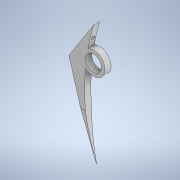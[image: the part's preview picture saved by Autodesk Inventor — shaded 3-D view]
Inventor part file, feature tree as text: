
AUTODESK INVENTOR PART (.ipt)
format: ipt  version: 2022 (Build 260153000, 153)  size: 128,000 bytes
history: native  units: in
note: dims shown in document units (in); Inventor stores cm internally (conversion verified against a paired STEP export)
features: extrude x3, sketch x3
ambient origin geometry x8: Origin, YZ Plane, XZ Plane, XY Plane, X Axis, Y Axis, Z Axis, Center Point
bodies: Solid1 (feature_tree)
feature tree (6):
  extrude  "Extrusion1"  Depth=0.75in
  extrude  "Extrusion2"  Depth=0.5909in
  extrude  "Extrusion3"  Depth=1.0125in TaperAngle=0.0deg
  sketch  "Sketch1"  dims[d0=0.52in d1=0.75in]
  sketch  "Sketch2"  dims[d2=0.2in d3=0.0in d4=0.5909in]
  sketch  "Sketch3"  dims[d5=0.5909in d6=1.0125in d7=0.0in d8=0.1in d9=1.0125in d10=0.0in]
